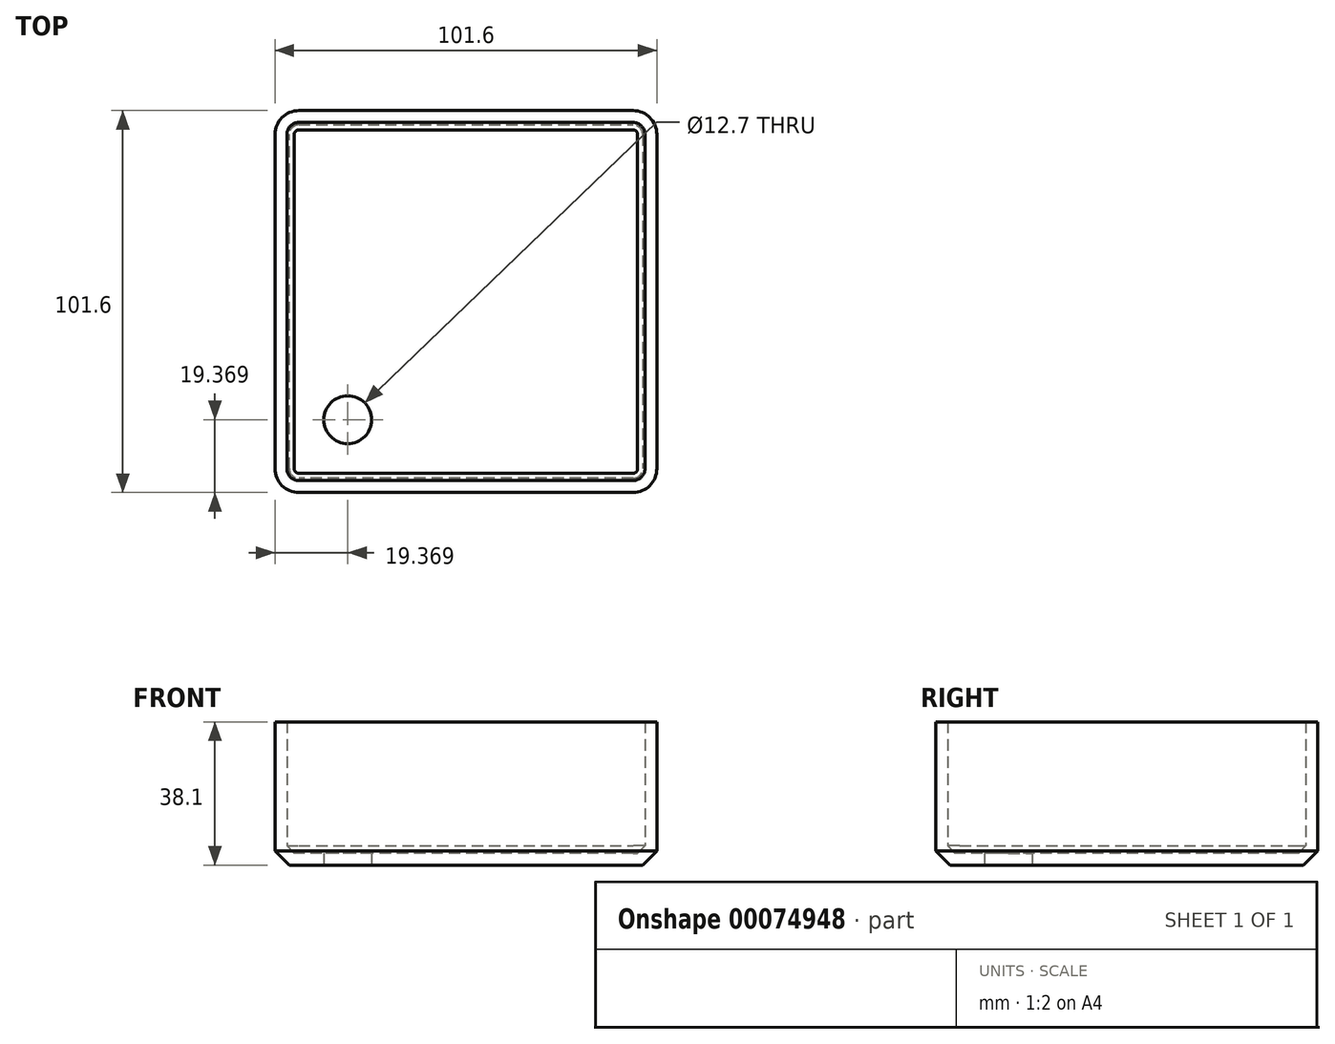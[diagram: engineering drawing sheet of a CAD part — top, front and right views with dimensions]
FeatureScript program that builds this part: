
annotation { "Feature Type Name" : "Feature", "Feature Type Description" : "" }
export const myFeature = defineFeature(function(context is Context, id is Id, definition is map)
    precondition{}
    {
        {
            var Q0;
            Q0=qCreatedBy(makeId("Top.planeOp"),FACE);
            var sketch = newSketch(context, id + "F0", { "sketchPlane" : qUnion([Q0])});
            skLineSegment(sketch, "E0.rect.bottom", {"start": v(50.8, 50.8) * mm, "end": v(-50.8, 50.8) * mm});
            skLineSegment(sketch, "E0.rect.top", {"start": v(50.8, -50.8) * mm, "end": v(-50.8, -50.8) * mm});
            skLineSegment(sketch, "E0.rect.left", {"start": v(50.8, 50.8) * mm, "end": v(50.8, -50.8) * mm});
            skLineSegment(sketch, "E0.rect.right", {"start": v(-50.8, 50.8) * mm, "end": v(-50.8, -50.8) * mm});
            skPoint(sketch, "E0.rect.middle", {"position": v(0, 0) * mm});
            skSolve(sketch);
        }
        {
            var Q0;
            Q0 = qSketchRegion(id + "F0", true);
            extrude(context, id + "F1", {"entities" : qUnion([Q0]), "depth" : 38.1 * mm});
        }
        {
            var Q0;
            Q0=makeQuery(id+"F1.opExtrude","CAP_FACE",FACE,{"disambiguationData":[OSD([sQuery(id+"F0.wireOp",EDGE,"E0.rect.bottom"),sQuery(id+"F0.wireOp",EDGE,"E0.rect.top"),sQuery(id+"F0.wireOp",EDGE,"E0.rect.left"),sQuery(id+"F0.wireOp",EDGE,"E0.rect.right")])],"isStart":true});
            var sketch = newSketch(context, id + "F2", { "sketchPlane" : qUnion([Q0])});
            skCircle(sketch, "E1", {"center": v(-31.43, 31.43) * mm, "radius": 6.35 * mm});
            skLineSegment(sketch, "E2", {"start": v(-31.43, 31.43) * mm, "end": v(0, 0) * mm, "construction": true});
            skSolve(sketch);
        }
        {
            var Q0;
            Q0=makeQuery(id+"F1.opExtrude","SWEPT_EDGE",EDGE,{"disambiguationData":[OSD([sQuery(id+"F0.wireOp",EDGE,"E0.rect.bottom"),sQuery(id+"F0.wireOp",EDGE,"E0.rect.right")])]});
            var Q1;
            Q1=makeQuery(id+"F1.opExtrude","SWEPT_EDGE",EDGE,{"disambiguationData":[OSD([sQuery(id+"F0.wireOp",EDGE,"E0.rect.top"),sQuery(id+"F0.wireOp",EDGE,"E0.rect.left")])]});
            var Q2;
            Q2=makeQuery(id+"F1.opExtrude","SWEPT_EDGE",EDGE,{"disambiguationData":[OSD([sQuery(id+"F0.wireOp",EDGE,"E0.rect.bottom"),sQuery(id+"F0.wireOp",EDGE,"E0.rect.left")])]});
            var Q3;
            Q3=makeQuery(id+"F1.opExtrude","SWEPT_EDGE",EDGE,{"disambiguationData":[OSD([sQuery(id+"F0.wireOp",EDGE,"E0.rect.top"),sQuery(id+"F0.wireOp",EDGE,"E0.rect.right")])]});
            fillet(context, id + "F3", {"entities" : qUnion([Q0, Q1, Q2, Q3]), "radius" : 6.35 * mm, "tangentPropagation" : true, "allowEdgeOverflow" : false});
        }
        {
            var Q0;
            Q0=makeQuery(id+"F1.opExtrude","CAP_EDGE",EDGE,{"disambiguationData":[OSD([sQuery(id+"F0.wireOp",EDGE,"E0.rect.top")])],"isStart":true});
            chamfer(context, id + "F4", {"entities" : qUnion([Q0]), "width" : 3.8 * mm, "tangentPropagation" : true});
        }
        {
            var Q0;
            Q0=makeQuery(id+"F1.opExtrude","CAP_FACE",FACE,{"disambiguationData":[OSD([sQuery(id+"F0.wireOp",EDGE,"E0.rect.bottom"),sQuery(id+"F0.wireOp",EDGE,"E0.rect.top"),sQuery(id+"F0.wireOp",EDGE,"E0.rect.left"),sQuery(id+"F0.wireOp",EDGE,"E0.rect.right")])],"isStart":false});
            shell(context, id + "F5", {"entities" : qUnion([Q0]), "thickness" : 3.17 * mm});
        }
        {
            var Q0;
            Q0 = qSketchRegion(id + "F2", true);
            extrude(context, id + "F6", {"entities" : qUnion([Q0]), "operationType" : NewBodyOperationType.REMOVE, "endBound" : BoundingType.THROUGH_ALL, "oppositeDirection" : true, "depth" : 25.4 * mm});
        }
    });
